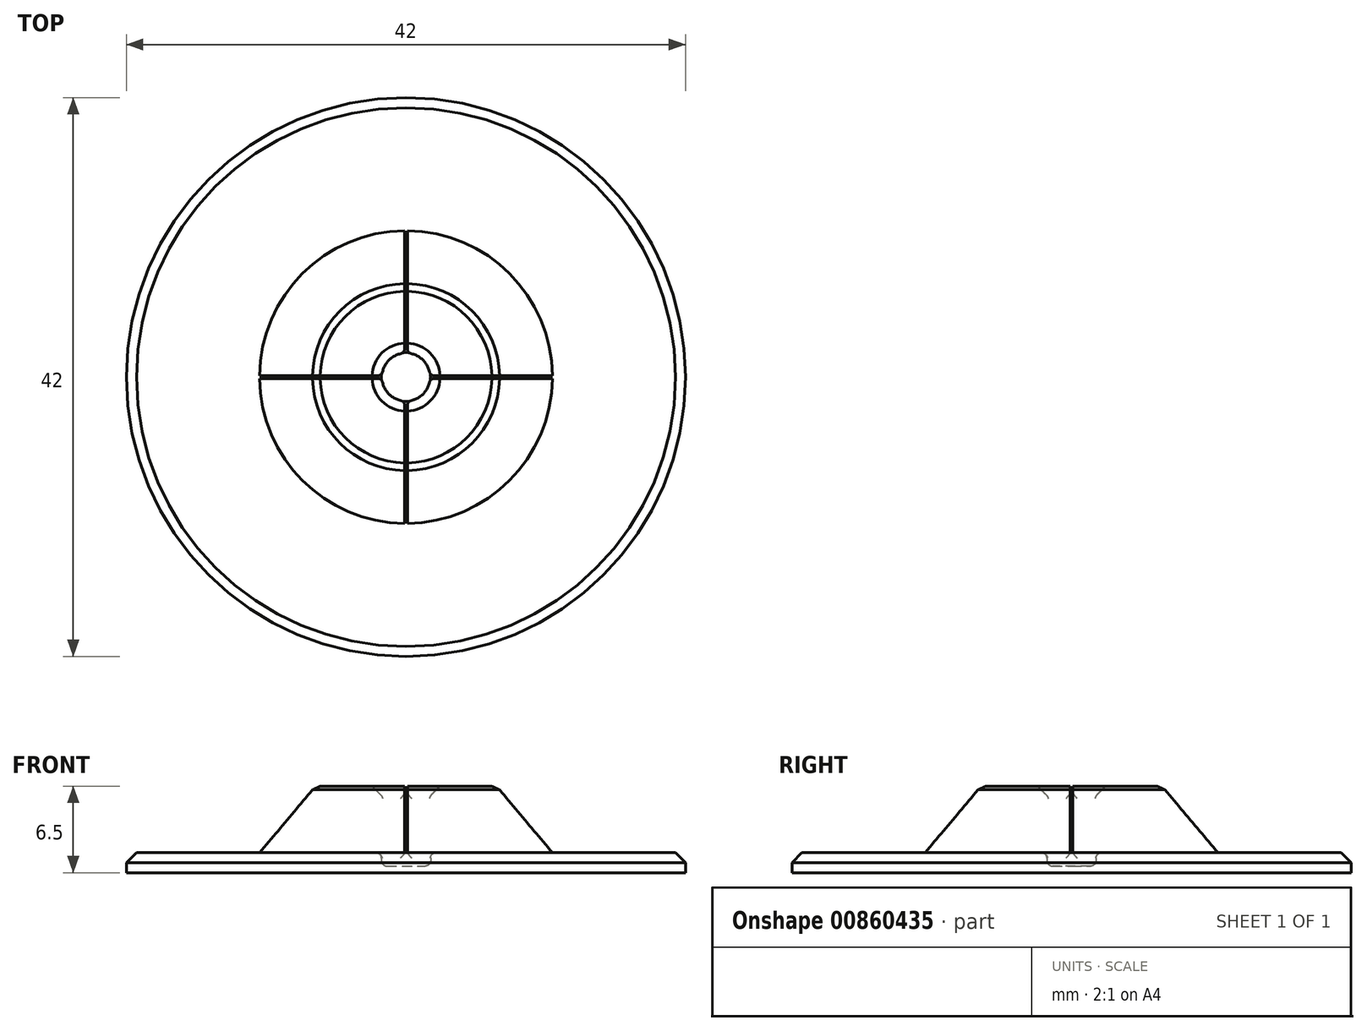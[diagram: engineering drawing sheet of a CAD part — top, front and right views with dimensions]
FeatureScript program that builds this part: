
annotation { "Feature Type Name" : "Feature", "Feature Type Description" : "" }
export const myFeature = defineFeature(function(context is Context, id is Id, definition is map)
    precondition{}
    {
        {
            var Q0;
            Q0=qCreatedBy(makeId("Front.planeOp"),FACE);
            var sketch = newSketch(context, id + "F0", { "sketchPlane" : qUnion([Q0])});
            skLineSegment(sketch, "E0", {"start": v(0, 0) * mm, "end": v(-21, 0) * mm});
            skLineSegment(sketch, "E1", {"start": v(-21, 0) * mm, "end": v(-21, 1.5) * mm});
            skLineSegment(sketch, "E2", {"start": v(-21, 1.5) * mm, "end": v(-11, 1.5) * mm});
            skLineSegment(sketch, "E3", {"start": v(-11, 1.5) * mm, "end": v(-6.8, 6.5) * mm});
            skLineSegment(sketch, "E4", {"start": v(-6.8, 6.5) * mm, "end": v(-1.8, 6.5) * mm});
            skLineSegment(sketch, "E5", {"start": v(-1.8, 6.5) * mm, "end": v(-1.85, 0.5) * mm});
            skLineSegment(sketch, "E6", {"start": v(-1.85, 0.5) * mm, "end": v(0, 0.5) * mm});
            skLineSegment(sketch, "E7", {"start": v(0, 13.11) * mm, "end": v(0, -12.42) * mm, "construction": true});
            skLineSegment(sketch, "E8", {"start": v(0, 0.5) * mm, "end": v(0, 0) * mm});
            skSolve(sketch);
        }
        {
            var Q0;
            Q0=makeQuery(id+"F0.imprint","IMPRINT",FACE,{"disambiguationData":[TD([[makeQuery(id+"F0.imprint","IMPRINT",EDGE,{"derivedFrom":sQuery(id+"F0.wireOp",EDGE,"E0")}),-1.0]])]});
            var Q1;
            Q1=sQuery(id+"F0.wireOp",EDGE,"E7");
            revolve(context, id + "F1", {"surfaceOperationType" : NewSurfaceOperationType.NEW, "entities" : qUnion([Q0]), "axis" : qUnion([Q1]), "revolveType" : RevolveType.FULL});
        }
        {
            var Q0;
            Q0=makeQuery(id+"F1.opRevolve","SWEPT_FACE",FACE,{"disambiguationData":[OSD([sQuery(id+"F0.wireOp",EDGE,"E4")])]});
            var sketch = newSketch(context, id + "F2", { "sketchPlane" : qUnion([Q0])});
            skLineSegment(sketch, "E9", {"start": v(-11.35, 0) * mm, "end": v(11.56, 0) * mm, "construction": true});
            skLineSegment(sketch, "E10", {"start": v(0, -11.49) * mm, "end": v(0, 12.04) * mm, "construction": true});
            skLineSegment(sketch, "E11.0", {"start": v(-11.35, -0.1) * mm, "end": v(11.56, -0.1) * mm});
            skLineSegment(sketch, "E12.0", {"start": v(-11.35, 0.1) * mm, "end": v(11.56, 0.1) * mm});
            skLineSegment(sketch, "E13.0", {"start": v(0.1, -11.49) * mm, "end": v(0.1, 12.04) * mm});
            skLineSegment(sketch, "E14.0", {"start": v(-0.1, -11.49) * mm, "end": v(-0.1, 12.04) * mm});
            skLineSegment(sketch, "E15", {"start": v(-11.35, -0.1) * mm, "end": v(-11.35, 0.1) * mm});
            skLineSegment(sketch, "E16", {"start": v(11.56, -0.1) * mm, "end": v(11.56, 0.1) * mm});
            skLineSegment(sketch, "E17", {"start": v(-0.1, -11.49) * mm, "end": v(0.1, -11.49) * mm});
            skLineSegment(sketch, "E18", {"start": v(-0.1, 12.04) * mm, "end": v(0.1, 12.04) * mm});
            skSolve(sketch);
        }
        {
            var Q0;
            {var subQ0=sQuery(id+"F2.wireOp",EDGE,"E15");Q0=makeQuery(id+"F2.imprint","IMPRINT",FACE,{"disambiguationData":[TD([[makeQuery(id+"F2.imprint","IMPRINT",EDGE,{"derivedFrom":subQ0}),-1.0]])]});}
            var Q1;
            {var subQ0=sQuery(id+"F2.wireOp",EDGE,"E11.0");var subQ1=sQuery(id+"F0.wireOp",EDGE,"E4");var subQ2=makeQuery(id+"F1.opRevolve","SWEPT_EDGE",EDGE,{"disambiguationData":[OSD([sQuery(id+"F0.wireOp",EDGE,"E3"),subQ1])]});var subQ3=makeQuery(id+"F2.imprint","INTERSECT",VERTEX,{"disambiguationData":[OD(0.0)],"derivedFrom":[subQ2,subQ0]});Q1=makeQuery(id+"F2.imprint","IMPRINT",FACE,{"disambiguationData":[TD([[makeQuery(id+"F2.imprint","IMPRINT",EDGE,{"disambiguationData":[TD([[subQ3,-1.0]])],"derivedFrom":subQ0}),1.0]])]});}
            var Q2;
            {var subQ0=sQuery(id+"F2.wireOp",EDGE,"E11.0");var subQ1=sQuery(id+"F0.wireOp",EDGE,"E4");var subQ2=makeQuery(id+"F1.opRevolve","SWEPT_EDGE",EDGE,{"disambiguationData":[OSD([sQuery(id+"F0.wireOp",EDGE,"E3"),subQ1])]});var subQ3=makeQuery(id+"F2.imprint","INTERSECT",VERTEX,{"disambiguationData":[OD(1.0)],"derivedFrom":[subQ2,subQ0]});Q2=makeQuery(id+"F2.imprint","IMPRINT",FACE,{"disambiguationData":[TD([[makeQuery(id+"F2.imprint","IMPRINT",EDGE,{"disambiguationData":[TD([[subQ3,1.0]])],"derivedFrom":subQ0}),1.0]])]});}
            var Q3;
            {var subQ0=sQuery(id+"F2.wireOp",EDGE,"E16");Q3=makeQuery(id+"F2.imprint","IMPRINT",FACE,{"disambiguationData":[TD([[makeQuery(id+"F2.imprint","IMPRINT",EDGE,{"derivedFrom":subQ0}),1.0]])]});}
            var Q4;
            {var subQ0=sQuery(id+"F2.wireOp",EDGE,"E13.0");var subQ1=sQuery(id+"F0.wireOp",EDGE,"E4");var subQ2=makeQuery(id+"F1.opRevolve","SWEPT_EDGE",EDGE,{"disambiguationData":[OSD([sQuery(id+"F0.wireOp",EDGE,"E3"),subQ1])]});var subQ3=makeQuery(id+"F2.imprint","INTERSECT",VERTEX,{"disambiguationData":[OD(1.0)],"derivedFrom":[subQ2,subQ0]});Q4=makeQuery(id+"F2.imprint","IMPRINT",FACE,{"disambiguationData":[TD([[makeQuery(id+"F2.imprint","IMPRINT",EDGE,{"disambiguationData":[TD([[subQ3,1.0]])],"derivedFrom":subQ0}),1.0]])]});}
            var Q5;
            {var subQ0=sQuery(id+"F2.wireOp",EDGE,"E13.0");var subQ1=sQuery(id+"F0.wireOp",EDGE,"E4");var subQ2=makeQuery(id+"F1.opRevolve","SWEPT_EDGE",EDGE,{"disambiguationData":[OSD([sQuery(id+"F0.wireOp",EDGE,"E3"),subQ1])]});var subQ3=makeQuery(id+"F2.imprint","INTERSECT",VERTEX,{"disambiguationData":[OD(0.0)],"derivedFrom":[subQ2,subQ0]});Q5=makeQuery(id+"F2.imprint","IMPRINT",FACE,{"disambiguationData":[TD([[makeQuery(id+"F2.imprint","IMPRINT",EDGE,{"disambiguationData":[TD([[subQ3,-1.0]])],"derivedFrom":subQ0}),1.0]])]});}
            var Q6;
            {var subQ0=sQuery(id+"F2.wireOp",EDGE,"E17");Q6=makeQuery(id+"F2.imprint","IMPRINT",FACE,{"disambiguationData":[TD([[makeQuery(id+"F2.imprint","IMPRINT",EDGE,{"derivedFrom":subQ0}),1.0]])]});}
            var Q7;
            {var subQ0=sQuery(id+"F2.wireOp",EDGE,"E18");Q7=makeQuery(id+"F2.imprint","IMPRINT",FACE,{"disambiguationData":[TD([[makeQuery(id+"F2.imprint","IMPRINT",EDGE,{"derivedFrom":subQ0}),-1.0]])]});}
            extrude(context, id + "F3", {"entities" : qUnion([Q0, Q1, Q2, Q3, Q4, Q5, Q6, Q7]), "operationType" : NewBodyOperationType.REMOVE, "oppositeDirection" : true, "depth" : 5 * mm, "offsetDistance" : 25 * mm});
        }
        {
            var Q0;
            {var subQ0=sQuery(id+"F0.wireOp",EDGE,"E4");var subQ1=sQuery(id+"F0.wireOp",EDGE,"E5");var subQ2=sQuery(id+"F2.wireOp",EDGE,"E11.0");var subQ3=makeQuery(id+"F1.opRevolve","SWEPT_EDGE",EDGE,{"disambiguationData":[OSD([sQuery(id+"F0.wireOp",EDGE,"E3"),subQ0])]});var subQ4=makeQuery(id+"F2.imprint","INTERSECT",VERTEX,{"disambiguationData":[OD(0.0)],"derivedFrom":[subQ3,subQ2]});var subQ5=makeQuery(id+"F1.opRevolve","SWEPT_EDGE",EDGE,{"disambiguationData":[OSD([subQ0,subQ1])]});Q0=makeQuery(id+"F3.boolean.opBoolean","SPLIT",EDGE,{"disambiguationData":[TD([makeQuery(id+"F3.opExtrude","SWEPT_FACE",FACE,{"disambiguationData":[OSD([subQ2]),TDD([makeQuery(id+"F2.imprint","IMPRINT",EDGE,{"disambiguationData":[TD([[makeQuery(id+"F2.imprint","INTERSECT",VERTEX,{"derivedFrom":[subQ2,sQuery(id+"F2.wireOp",EDGE,"E15")]}),-1.0]])],"derivedFrom":subQ2}),makeQuery(id+"F2.imprint","IMPRINT",EDGE,{"disambiguationData":[TD([[subQ4,-1.0]])],"derivedFrom":subQ2})])]})])],"derivedFrom":subQ5});}
            var Q1;
            {var subQ0=sQuery(id+"F0.wireOp",EDGE,"E4");var subQ2=makeQuery(id+"F1.opRevolve","SWEPT_EDGE",EDGE,{"disambiguationData":[OSD([sQuery(id+"F0.wireOp",EDGE,"E3"),subQ0])]});var subQ4=sQuery(id+"F0.wireOp",EDGE,"E5");var subQ5=makeQuery(id+"F1.opRevolve","SWEPT_EDGE",EDGE,{"disambiguationData":[OSD([subQ0,subQ4])]});var subQ6=sQuery(id+"F2.wireOp",EDGE,"E14.0");Q1=makeQuery(id+"F3.boolean.opBoolean","SPLIT",EDGE,{"disambiguationData":[TD([makeQuery(id+"F3.opExtrude","SWEPT_FACE",FACE,{"disambiguationData":[OSD([subQ6]),TDD([makeQuery(id+"F2.imprint","IMPRINT",EDGE,{"disambiguationData":[TD([[makeQuery(id+"F2.imprint","INTERSECT",VERTEX,{"disambiguationData":[OD(1.0)],"derivedFrom":[subQ2,subQ6]}),1.0]])],"derivedFrom":subQ6})])]})])],"derivedFrom":subQ5});}
            var Q2;
            {var subQ0=sQuery(id+"F0.wireOp",EDGE,"E4");var subQ1=sQuery(id+"F2.wireOp",EDGE,"E13.0");var subQ2=makeQuery(id+"F1.opRevolve","SWEPT_EDGE",EDGE,{"disambiguationData":[OSD([sQuery(id+"F0.wireOp",EDGE,"E3"),subQ0])]});var subQ3=sQuery(id+"F0.wireOp",EDGE,"E5");var subQ4=makeQuery(id+"F1.opRevolve","SWEPT_EDGE",EDGE,{"disambiguationData":[OSD([subQ0,subQ3])]});Q2=makeQuery(id+"F3.boolean.opBoolean","SPLIT",EDGE,{"disambiguationData":[TD([makeQuery(id+"F3.opExtrude","SWEPT_FACE",FACE,{"disambiguationData":[OSD([subQ1]),TDD([makeQuery(id+"F2.imprint","IMPRINT",EDGE,{"disambiguationData":[TD([[makeQuery(id+"F2.imprint","INTERSECT",VERTEX,{"disambiguationData":[OD(1.0)],"derivedFrom":[subQ2,subQ1]}),1.0]])],"derivedFrom":subQ1})])]})])],"derivedFrom":subQ4});}
            var Q3;
            {var subQ0=sQuery(id+"F0.wireOp",EDGE,"E4");var subQ1=sQuery(id+"F0.wireOp",EDGE,"E5");var subQ2=sQuery(id+"F2.wireOp",EDGE,"E11.0");var subQ3=makeQuery(id+"F1.opRevolve","SWEPT_EDGE",EDGE,{"disambiguationData":[OSD([sQuery(id+"F0.wireOp",EDGE,"E3"),subQ0])]});var subQ4=makeQuery(id+"F2.imprint","INTERSECT",VERTEX,{"disambiguationData":[OD(1.0)],"derivedFrom":[subQ3,subQ2]});var subQ5=makeQuery(id+"F1.opRevolve","SWEPT_EDGE",EDGE,{"disambiguationData":[OSD([subQ0,subQ1])]});Q3=makeQuery(id+"F3.boolean.opBoolean","SPLIT",EDGE,{"disambiguationData":[TD([makeQuery(id+"F3.opExtrude","SWEPT_FACE",FACE,{"disambiguationData":[OSD([subQ2]),TDD([makeQuery(id+"F2.imprint","IMPRINT",EDGE,{"disambiguationData":[TD([[subQ4,1.0]])],"derivedFrom":subQ2}),makeQuery(id+"F2.imprint","IMPRINT",EDGE,{"disambiguationData":[TD([[makeQuery(id+"F2.imprint","INTERSECT",VERTEX,{"derivedFrom":[subQ2,sQuery(id+"F2.wireOp",EDGE,"E16")]}),1.0]])],"derivedFrom":subQ2})])]})])],"derivedFrom":subQ5});}
            var Q4;
            Q4=makeQuery(id+"F1.opRevolve","SWEPT_EDGE",EDGE,{"disambiguationData":[OSD([sQuery(id+"F0.wireOp",EDGE,"E1"),sQuery(id+"F0.wireOp",EDGE,"E2")])]});
            var Q5;
            {var subQ0=sQuery(id+"F0.wireOp",EDGE,"E3");var subQ1=sQuery(id+"F0.wireOp",EDGE,"E4");var subQ2=sQuery(id+"F2.wireOp",EDGE,"E11.0");var subQ3=makeQuery(id+"F1.opRevolve","SWEPT_EDGE",EDGE,{"disambiguationData":[OSD([subQ0,subQ1])]});var subQ4=makeQuery(id+"F2.imprint","INTERSECT",VERTEX,{"disambiguationData":[OD(1.0)],"derivedFrom":[subQ3,subQ2]});Q5=makeQuery(id+"F3.boolean.opBoolean","SPLIT",EDGE,{"disambiguationData":[TD([makeQuery(id+"F3.opExtrude","SWEPT_FACE",FACE,{"disambiguationData":[OSD([subQ2]),TDD([makeQuery(id+"F2.imprint","IMPRINT",EDGE,{"disambiguationData":[TD([[subQ4,1.0]])],"derivedFrom":subQ2}),makeQuery(id+"F2.imprint","IMPRINT",EDGE,{"disambiguationData":[TD([[makeQuery(id+"F2.imprint","INTERSECT",VERTEX,{"derivedFrom":[subQ2,sQuery(id+"F2.wireOp",EDGE,"E16")]}),1.0]])],"derivedFrom":subQ2})])]})])],"derivedFrom":subQ3});}
            var Q6;
            {var subQ0=sQuery(id+"F0.wireOp",EDGE,"E3");var subQ1=sQuery(id+"F2.wireOp",EDGE,"E11.0");var subQ2=sQuery(id+"F0.wireOp",EDGE,"E4");var subQ3=makeQuery(id+"F1.opRevolve","SWEPT_EDGE",EDGE,{"disambiguationData":[OSD([subQ0,subQ2])]});var subQ4=makeQuery(id+"F2.imprint","INTERSECT",VERTEX,{"disambiguationData":[OD(0.0)],"derivedFrom":[subQ3,subQ1]});Q6=makeQuery(id+"F3.boolean.opBoolean","SPLIT",EDGE,{"disambiguationData":[TD([makeQuery(id+"F3.opExtrude","SWEPT_FACE",FACE,{"disambiguationData":[OSD([subQ1]),TDD([makeQuery(id+"F2.imprint","IMPRINT",EDGE,{"disambiguationData":[TD([[makeQuery(id+"F2.imprint","INTERSECT",VERTEX,{"derivedFrom":[subQ1,sQuery(id+"F2.wireOp",EDGE,"E15")]}),-1.0]])],"derivedFrom":subQ1}),makeQuery(id+"F2.imprint","IMPRINT",EDGE,{"disambiguationData":[TD([[subQ4,-1.0]])],"derivedFrom":subQ1})])]})])],"derivedFrom":subQ3});}
            var Q7;
            {var subQ1=sQuery(id+"F0.wireOp",EDGE,"E4");var subQ2=sQuery(id+"F0.wireOp",EDGE,"E3");var subQ3=makeQuery(id+"F1.opRevolve","SWEPT_EDGE",EDGE,{"disambiguationData":[OSD([subQ2,subQ1])]});var subQ6=sQuery(id+"F2.wireOp",EDGE,"E14.0");Q7=makeQuery(id+"F3.boolean.opBoolean","SPLIT",EDGE,{"disambiguationData":[TD([makeQuery(id+"F3.opExtrude","SWEPT_FACE",FACE,{"disambiguationData":[OSD([subQ6]),TDD([makeQuery(id+"F2.imprint","IMPRINT",EDGE,{"disambiguationData":[TD([[makeQuery(id+"F2.imprint","INTERSECT",VERTEX,{"disambiguationData":[OD(1.0)],"derivedFrom":[subQ3,subQ6]}),1.0]])],"derivedFrom":subQ6})])]})])],"derivedFrom":subQ3});}
            var Q8;
            {var subQ1=sQuery(id+"F0.wireOp",EDGE,"E4");var subQ2=sQuery(id+"F0.wireOp",EDGE,"E3");var subQ3=makeQuery(id+"F1.opRevolve","SWEPT_EDGE",EDGE,{"disambiguationData":[OSD([subQ2,subQ1])]});var subQ6=sQuery(id+"F2.wireOp",EDGE,"E13.0");Q8=makeQuery(id+"F3.boolean.opBoolean","SPLIT",EDGE,{"disambiguationData":[TD([makeQuery(id+"F3.opExtrude","SWEPT_FACE",FACE,{"disambiguationData":[OSD([subQ6]),TDD([makeQuery(id+"F2.imprint","IMPRINT",EDGE,{"disambiguationData":[TD([[makeQuery(id+"F2.imprint","INTERSECT",VERTEX,{"disambiguationData":[OD(1.0)],"derivedFrom":[subQ3,subQ6]}),1.0]])],"derivedFrom":subQ6})])]})])],"derivedFrom":subQ3});}
            chamfer(context, id + "F4", {"entities" : qUnion([Q0, Q1, Q2, Q3, Q4, Q5, Q6, Q7, Q8]), "width" : 0.75 * mm, "tangentPropagation" : true});
        }
        {
            var Q0;
            {var subQ0=sQuery(id+"F2.wireOp",EDGE,"E12.0");var subQ1=sQuery(id+"F0.wireOp",EDGE,"E4");var subQ2=makeQuery(id+"F2.imprint","INTERSECT",VERTEX,{"disambiguationData":[OD(1.0)],"derivedFrom":[makeQuery(id+"F1.opRevolve","SWEPT_EDGE",EDGE,{"disambiguationData":[OSD([sQuery(id+"F0.wireOp",EDGE,"E3"),subQ1])]}),subQ0]});var subQ3=sQuery(id+"F0.wireOp",EDGE,"E5");Q0=makeQuery(id+"F3.boolean.opBoolean","INTERSECT",EDGE,{"derivedFrom":[makeQuery(id+"F1.opRevolve","SWEPT_FACE",FACE,{"disambiguationData":[OSD([subQ3])]}),makeQuery(id+"F3.opExtrude","SWEPT_FACE",FACE,{"disambiguationData":[OSD([subQ0]),TDD([makeQuery(id+"F2.imprint","IMPRINT",EDGE,{"disambiguationData":[TD([[subQ2,1.0]])],"derivedFrom":subQ0}),makeQuery(id+"F2.imprint","IMPRINT",EDGE,{"disambiguationData":[TD([[makeQuery(id+"F2.imprint","INTERSECT",VERTEX,{"derivedFrom":[subQ0,sQuery(id+"F2.wireOp",EDGE,"E16")]}),1.0]])],"derivedFrom":subQ0})])]})]});}
            var Q1;
            Q1=makeQuery(id+"F1.opRevolve","SWEPT_FACE",FACE,{"disambiguationData":[OSD([sQuery(id+"F0.wireOp",EDGE,"E5")])]});
            fillet(context, id + "F5", {"entities" : qUnion([Q0, Q1]), "radius" : 0.4 * mm, "tangentPropagation" : true, "allowEdgeOverflow" : false});
        }
    });
